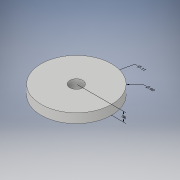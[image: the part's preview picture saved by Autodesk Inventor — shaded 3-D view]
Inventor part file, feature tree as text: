
AUTODESK INVENTOR PART (.ipt)
format: ipt  version: 2018 (Build 220112000, 112)  size: 110,592 bytes
history: native  units: in
note: dims shown in document units (in); Inventor stores cm internally (conversion verified against a paired STEP export)
features: other x4, sketch x2, extrude x1, hole x1
ambient origin geometry x8: Origin, YZ Plane, XZ Plane, XY Plane, X Axis, Y Axis, Z Axis, Center Point
bodies: Solid1 (feature_tree)
feature tree (8):
  other  "Annotations"
  extrude  "Extrusion1"  Depth=0.08in TaperAngle=0.0deg
  hole  "Hole1"  [1 undecoded]
  sketch  "Sketch1"  dims[d0=0.6in d1=0.08in d2=0.0in]
  sketch  "Sketch2"  dims[d3=0.11in d4=0.11in d5=0.75in d6=0.375in d7=0.25in d8=0.5635in d9=1.0in d10=0.8108in d11=0.08in d12=1.9758in d13=0.0604in d14=0.323in d15=0.11in d16=1.8817in d17=0.3937in d18=0.2212in d19=0.6in]
  other  "Linear Dimension 1"
  other  "Diameter Dimension 1"
  other  "Diameter Dimension 2"
note: 1 required parameter value undecoded (feature->parameter linkage not recoverable at this tier; creation-order binding heuristic only, values carry confidence <= 0.55)
